# Revit family: PRD_AR_WCFlshngVlvs_R3SystemBox_F3BF40011
name_source: partatom
category: Specialty Equipment
units: mm (PartAtom-declared; Revit-internal decimal feet)

## family parameters
Cut with Voids When Loaded = Yes
Enable Cutting in Views = Yes
Host = Face
Maintain Annotation Orientation = No
OmniClass Number = 23.45.05.14.99
OmniClass Title = Other Sanitary Washing Plumbing Fixtures
Part Type = Normal
Room Calculation Point = No
Round Connector Dimension = Use Diameter
Shared = No

## types (1)
- F3BF4001
    AssetType = Fixed
    BIMObjectName = PRD_AR_WCFlushingValves_R3SystemBox_F3BF4001
    BodyMaterial = PRD_AR_Plastic_Red
    BottomMaterial = PRD_AR_StainlessSteel_SatinFinished
    CW Connection = Yes
    CWFU = 0
    Category = Pr_40_20_93_91, WC flushing valves
    CloseOffRating = 0.0 Pa
    Color = Red
    Default Elevation = 1219 mm
    Description = R3 Basic installation kit for in-wall installation of finished installation kits for WC flushing valve DN 20. System box made of plastic, 174 x 225 mm, with screw connections, flush pipe connection, shell protection, flush connector for flushing and leak test, no stop valve.
    Export Type to IFC As = IfcValveType
    Features = System box made of plastic, 174 x 225 mm.
    FlowCoefficient = 0
    FlowColdWater = 0.0 L/s
    FlushingRate = 0.0 L/s
    HW Connection = Yes
    HWFU = 0
    IfcExportAs = IfcPipeFittingType
    IfcExportType = FLUSHING
    IsHighPressure = No
    Manufacturer = KWC Group Management AG
    ManufacturerName = KWC Group Management AG
    ManufacturerURL = www.kwc-professional.com
    Material = Plastic
    Model = F3BF4001
    ModelNumber = 2030068205
    ModelReference = F3BF4001
    NBSDescription = WC flushing valves
    NBSReference = 45-35-70/389
    Name = R3 System box F3BF4001
    NominalDepth = 0 mm  [stored 0 ft]
    NominalHeight = 225 mm  [stored 0.738189 ft]
    NominalWidth = 174 mm  [stored 0.570866 ft]
    ProductInformation = http://pim.kwc.com
    Size = 20
    Status = New
    TestPressure = 0.0 Pa
    Type IFC Predefined Type = FLUSHING
    URL = www.kwc-professional.com
    Uniclass2015Code = Pr_40_20_93_91
    Uniclass2015Title = WC flushing valves
    Uniclass2015Version = Products v1.36
    ValveMechanism = OTHER
    ValveOperation = OTHER
    ValvePattern = STRAIGHT_2_PORT
    Vent Connection = Yes
    Version = 1
    WFU = 0
    Waste Connection = Yes
    WorkingPressure = 0.0 Pa

note: [stored X ft] marks values corroborated as IEEE doubles in the binary element streams (Revit-internal decimal feet)

## geometry (parser evidence)
native form markers: Sweep x6
no freeform markers — native parametric forms only
